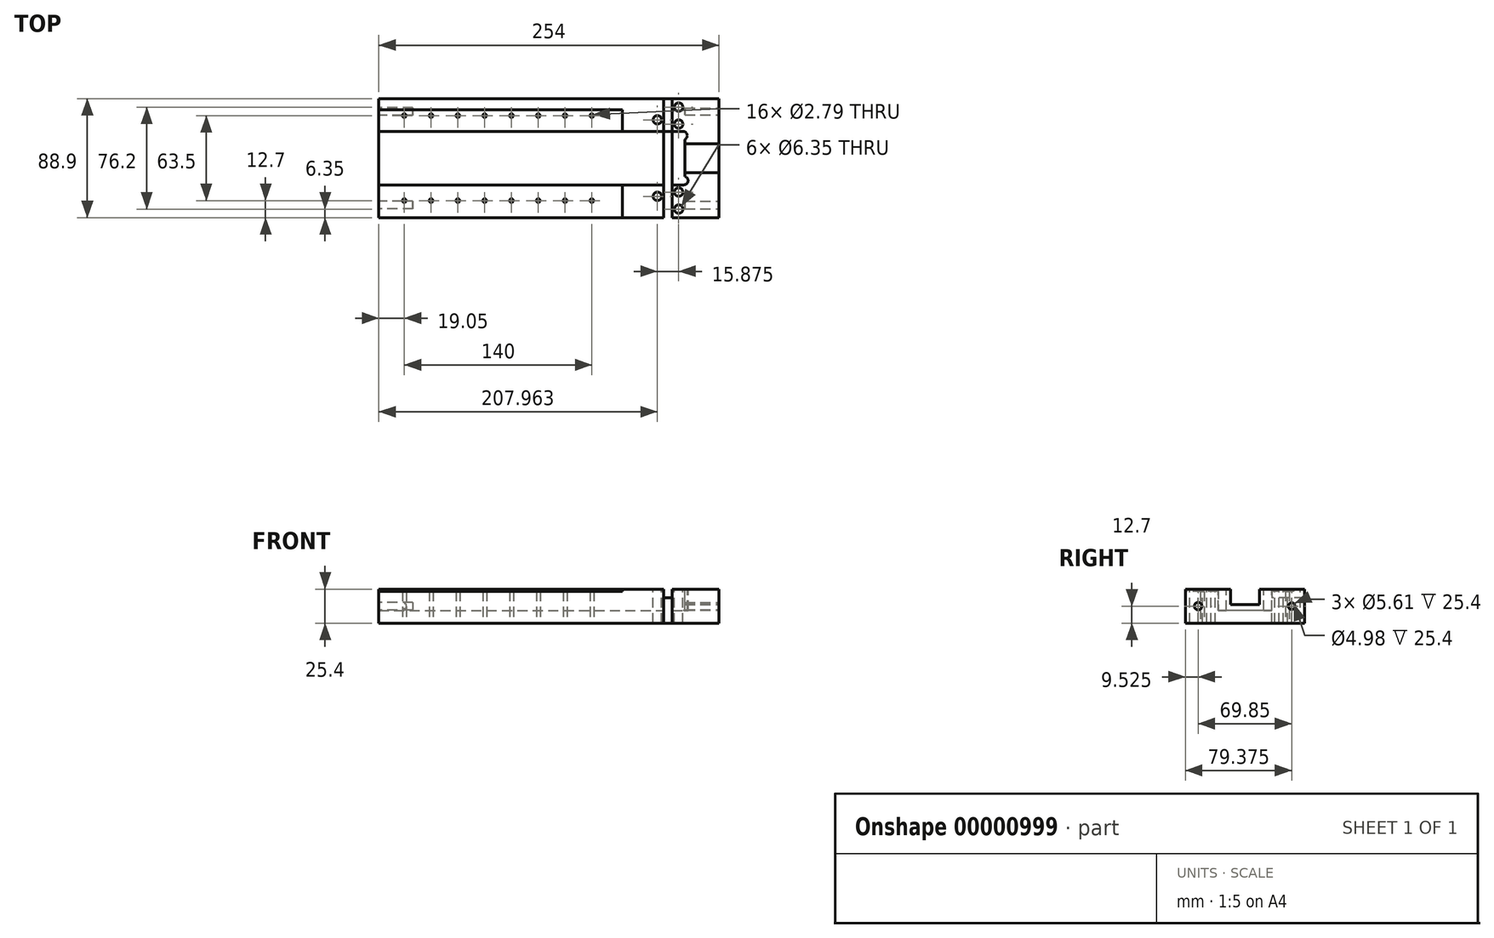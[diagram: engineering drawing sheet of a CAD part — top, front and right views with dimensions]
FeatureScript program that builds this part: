
annotation { "Feature Type Name" : "Feature", "Feature Type Description" : "" }
export const myFeature = defineFeature(function(context is Context, id is Id, definition is map)
    precondition{}
    {
        {
            var Q0;
            Q0=qCreatedBy(makeId("Top.planeOp"),FACE);
            var sketch = newSketch(context, id + "F0", { "sketchPlane" : qUnion([Q0])});
            skLineSegment(sketch, "E0.bottom", {"start": v(-127, 44.45) * mm, "end": v(127, 44.45) * mm});
            skLineSegment(sketch, "E0.top", {"start": v(-127, -44.45) * mm, "end": v(127, -44.45) * mm});
            skLineSegment(sketch, "E0.left", {"start": v(-127, 44.45) * mm, "end": v(-127, -44.45) * mm});
            skLineSegment(sketch, "E0.right", {"start": v(127, 44.45) * mm, "end": v(127, -44.45) * mm});
            skCircle(sketch, "E1", {"center": v(-107.95, -31.75) * mm, "radius": 1.4 * mm});
            skCircle(sketch, "E2", {"center": v(-107.95, 31.75) * mm, "radius": 1.4 * mm});
            skCircle(sketch, "E3", {"center": v(-27.95, 31.75) * mm, "radius": 1.4 * mm});
            skCircle(sketch, "E4", {"center": v(-87.95, 31.75) * mm, "radius": 1.4 * mm});
            skCircle(sketch, "E5", {"center": v(-67.95, 31.75) * mm, "radius": 1.4 * mm});
            skCircle(sketch, "E6", {"center": v(-47.95, 31.75) * mm, "radius": 1.4 * mm});
            skCircle(sketch, "E7", {"center": v(-7.95, 31.75) * mm, "radius": 1.4 * mm});
            skCircle(sketch, "E8", {"center": v(12.05, 31.75) * mm, "radius": 1.4 * mm});
            skCircle(sketch, "E9", {"center": v(32.05, 31.75) * mm, "radius": 1.4 * mm});
            skCircle(sketch, "E10", {"center": v(-87.95, -31.75) * mm, "radius": 1.4 * mm});
            skCircle(sketch, "E11", {"center": v(-67.95, -31.75) * mm, "radius": 1.4 * mm});
            skCircle(sketch, "E12", {"center": v(-47.95, -31.75) * mm, "radius": 1.4 * mm});
            skCircle(sketch, "E13", {"center": v(-27.95, -31.75) * mm, "radius": 1.4 * mm});
            skCircle(sketch, "E14", {"center": v(-7.95, -31.75) * mm, "radius": 1.4 * mm});
            skCircle(sketch, "E15", {"center": v(12.05, -31.75) * mm, "radius": 1.4 * mm});
            skCircle(sketch, "E16", {"center": v(32.05, -31.75) * mm, "radius": 1.4 * mm});
            skSolve(sketch);
        }
        {
            var Q0;
            Q0=makeQuery(id+"F0.imprint","IMPRINT",FACE,{"disambiguationData":[TD([[makeQuery(id+"F0.imprint","IMPRINT",EDGE,{"derivedFrom":sQuery(id+"F0.wireOp",EDGE,"E0.bottom")}),-1.0]])]});
            extrude(context, id + "F1", {"entities" : qUnion([Q0]), "depth" : 25.4 * mm});
        }
        {
            var Q0;
            Q0=makeQuery(id+"F1.opExtrude","CAP_FACE",FACE,{"disambiguationData":[OSD([sQuery(id+"F0.wireOp",EDGE,"E0.bottom"),sQuery(id+"F0.wireOp",EDGE,"E0.top"),sQuery(id+"F0.wireOp",EDGE,"E0.left"),sQuery(id+"F0.wireOp",EDGE,"E0.right"),sQuery(id+"F0.wireOp",EDGE,"E1"),sQuery(id+"F0.wireOp",EDGE,"E2"),sQuery(id+"F0.wireOp",EDGE,"E3"),sQuery(id+"F0.wireOp",EDGE,"E4"),sQuery(id+"F0.wireOp",EDGE,"E5"),sQuery(id+"F0.wireOp",EDGE,"E6"),sQuery(id+"F0.wireOp",EDGE,"E7"),sQuery(id+"F0.wireOp",EDGE,"E8"),sQuery(id+"F0.wireOp",EDGE,"E9"),sQuery(id+"F0.wireOp",EDGE,"E10"),sQuery(id+"F0.wireOp",EDGE,"E11"),sQuery(id+"F0.wireOp",EDGE,"E12"),sQuery(id+"F0.wireOp",EDGE,"E13"),sQuery(id+"F0.wireOp",EDGE,"E14"),sQuery(id+"F0.wireOp",EDGE,"E15"),sQuery(id+"F0.wireOp",EDGE,"E16")])],"isStart":false});
            var sketch = newSketch(context, id + "F2", { "sketchPlane" : qUnion([Q0])});
            skLineSegment(sketch, "E17.bottom", {"start": v(-127, 20) * mm, "end": v(100.1, 20) * mm});
            skLineSegment(sketch, "E17.top", {"start": v(-127, -20) * mm, "end": v(100.75, -20) * mm});
            skPoint(sketch, "E18.visualSharp", {"position": v(76.2, 20) * mm});
            skArc(sketch, "E18.filletArc", {"start": v(101.6, 14.02) * mm, "mid": v(103.18, 17.6) * mm, "end": v(100.1, 20) * mm});
            skPoint(sketch, "E19.visualSharp", {"position": v(76.2, -20) * mm});
            skArc(sketch, "E19.filletArc", {"start": v(100.75, -20) * mm, "mid": v(103.9, -17.25) * mm, "end": v(101.6, -13.77) * mm});
            skLineSegment(sketch, "E20", {"start": v(101.6, 14.02) * mm, "end": v(101.6, -13.77) * mm});
            skLineSegment(sketch, "E21", {"start": v(-127, 20) * mm, "end": v(-127, -20) * mm});
            skSolve(sketch);
        }
        {
            var Q0;
            Q0=makeQuery(id+"F2.imprint","IMPRINT",FACE,{"disambiguationData":[TD([[makeQuery(id+"F2.imprint","IMPRINT",EDGE,{"derivedFrom":sQuery(id+"F2.wireOp",EDGE,"E17.bottom")}),-1.0]])]});
            extrude(context, id + "F3", {"entities" : qUnion([Q0]), "operationType" : NewBodyOperationType.REMOVE, "oppositeDirection" : true, "depth" : 16 * mm});
        }
        {
            var Q0;
            Q0=makeQuery(id+"F1.opExtrude","CAP_FACE",FACE,{"disambiguationData":[OSD([sQuery(id+"F0.wireOp",EDGE,"E0.bottom"),sQuery(id+"F0.wireOp",EDGE,"E0.top"),sQuery(id+"F0.wireOp",EDGE,"E0.left"),sQuery(id+"F0.wireOp",EDGE,"E0.right"),sQuery(id+"F0.wireOp",EDGE,"E1"),sQuery(id+"F0.wireOp",EDGE,"E2"),sQuery(id+"F0.wireOp",EDGE,"E3"),sQuery(id+"F0.wireOp",EDGE,"E4"),sQuery(id+"F0.wireOp",EDGE,"E5"),sQuery(id+"F0.wireOp",EDGE,"E6"),sQuery(id+"F0.wireOp",EDGE,"E7"),sQuery(id+"F0.wireOp",EDGE,"E8"),sQuery(id+"F0.wireOp",EDGE,"E9"),sQuery(id+"F0.wireOp",EDGE,"E10"),sQuery(id+"F0.wireOp",EDGE,"E11"),sQuery(id+"F0.wireOp",EDGE,"E12"),sQuery(id+"F0.wireOp",EDGE,"E13"),sQuery(id+"F0.wireOp",EDGE,"E14"),sQuery(id+"F0.wireOp",EDGE,"E15"),sQuery(id+"F0.wireOp",EDGE,"E16")])],"isStart":false});
            var sketch = newSketch(context, id + "F4", { "sketchPlane" : qUnion([Q0])});
            skLineSegment(sketch, "E22.bottom", {"start": v(98.42, 10.8) * mm, "end": v(127, 10.8) * mm});
            skLineSegment(sketch, "E22.top", {"start": v(98.42, -10.8) * mm, "end": v(127, -10.8) * mm});
            skLineSegment(sketch, "E22.left", {"start": v(95.25, 7.62) * mm, "end": v(95.25, -7.62) * mm});
            skLineSegment(sketch, "E22.right", {"start": v(127, 10.8) * mm, "end": v(127, -10.8) * mm});
            skPoint(sketch, "E23.visualSharp", {"position": v(95.25, 10.8) * mm});
            skArc(sketch, "E23.filletArc", {"start": v(98.42, 10.8) * mm, "mid": v(96.18, 9.87) * mm, "end": v(95.25, 7.62) * mm});
            skPoint(sketch, "E24.visualSharp", {"position": v(95.25, -10.8) * mm});
            skArc(sketch, "E24.filletArc", {"start": v(95.25, -7.62) * mm, "mid": v(96.18, -9.87) * mm, "end": v(98.42, -10.8) * mm});
            skSolve(sketch);
        }
        {
            var Q0;
            {var subQ5=sQuery(id+"F4.wireOp",EDGE,"E22.right");Q0=makeQuery(id+"F4.imprint","IMPRINT",FACE,{"disambiguationData":[TD([[makeQuery(id+"F4.imprint","IMPRINT",EDGE,{"derivedFrom":subQ5}),-1.0]])]});}
            extrude(context, id + "F5", {"entities" : qUnion([Q0]), "operationType" : NewBodyOperationType.REMOVE, "oppositeDirection" : true, "depth" : 11.43 * mm});
        }
        {
            var Q0;
            {var subQ0=sQuery(id+"F0.wireOp",EDGE,"E0.bottom");var subQ1=sQuery(id+"F0.wireOp",EDGE,"E0.top");var subQ2=sQuery(id+"F0.wireOp",EDGE,"E0.left");var subQ3=sQuery(id+"F0.wireOp",EDGE,"E0.right");var subQ4=sQuery(id+"F0.wireOp",EDGE,"E1");var subQ5=sQuery(id+"F0.wireOp",EDGE,"E2");var subQ6=sQuery(id+"F0.wireOp",EDGE,"E3");var subQ7=sQuery(id+"F0.wireOp",EDGE,"E4");var subQ8=sQuery(id+"F0.wireOp",EDGE,"E5");var subQ9=sQuery(id+"F0.wireOp",EDGE,"E6");var subQ10=sQuery(id+"F0.wireOp",EDGE,"E7");var subQ11=sQuery(id+"F0.wireOp",EDGE,"E8");var subQ12=sQuery(id+"F0.wireOp",EDGE,"E9");var subQ13=sQuery(id+"F0.wireOp",EDGE,"E10");var subQ14=sQuery(id+"F0.wireOp",EDGE,"E11");var subQ15=sQuery(id+"F0.wireOp",EDGE,"E12");var subQ16=sQuery(id+"F0.wireOp",EDGE,"E13");var subQ17=sQuery(id+"F0.wireOp",EDGE,"E14");var subQ18=sQuery(id+"F0.wireOp",EDGE,"E15");var subQ19=sQuery(id+"F0.wireOp",EDGE,"E16");var subQ20=makeQuery(id+"F1.opExtrude","CAP_FACE",FACE,{"disambiguationData":[OSD([subQ0,subQ1,subQ2,subQ3,subQ4,subQ5,subQ6,subQ7,subQ8,subQ9,subQ10,subQ11,subQ12,subQ13,subQ14,subQ15,subQ16,subQ17,subQ18,subQ19])],"isStart":false});Q0=qUnion([makeQuery(id+"F5.boolean.opBoolean","SPLIT",FACE,{"disambiguationData":[TD([makeQuery(id+"F1.opExtrude","SWEPT_FACE",FACE,{"disambiguationData":[OSD([subQ0])]})])],"derivedFrom":subQ20}),makeQuery(id+"F5.boolean.opBoolean","SPLIT",FACE,{"disambiguationData":[TD([makeQuery(id+"F1.opExtrude","SWEPT_FACE",FACE,{"disambiguationData":[OSD([subQ1])]})])],"derivedFrom":subQ20})]);}
            var sketch = newSketch(context, id + "F6", { "sketchPlane" : qUnion([Q0])});
            skCircle(sketch, "E25", {"center": v(96.84, 38.1) * mm, "radius": 3.18 * mm});
            skLineSegment(sketch, "E26", {"start": v(76.2, 47.2) * mm, "end": v(76.2, -48.73) * mm, "construction": true});
            skCircle(sketch, "E27", {"center": v(80.96, 28.58) * mm, "radius": 3.18 * mm});
            skCircle(sketch, "E28", {"center": v(80.96, -28.57) * mm, "radius": 3.18 * mm});
            skCircle(sketch, "E29", {"center": v(96.84, -38.1) * mm, "radius": 3.18 * mm});
            skLineSegment(sketch, "E30", {"start": v(101.6, 52.36) * mm, "end": v(101.6, -69.51) * mm, "construction": true});
            skCircle(sketch, "E31", {"center": v(96.84, 25.4) * mm, "radius": 3.18 * mm});
            skCircle(sketch, "E32", {"center": v(96.84, -25.4) * mm, "radius": 3.18 * mm});
            skLineSegment(sketch, "E33.bottom", {"start": v(85.72, 46.37) * mm, "end": v(92.07, 46.37) * mm});
            skLineSegment(sketch, "E33.top", {"start": v(85.72, -47.17) * mm, "end": v(92.08, -47.17) * mm});
            skLineSegment(sketch, "E33.left", {"start": v(85.72, 46.37) * mm, "end": v(85.72, -47.17) * mm});
            skLineSegment(sketch, "E33.right", {"start": v(92.07, 46.37) * mm, "end": v(92.07, -47.17) * mm});
            skPoint(sketch, "E34", {"position": v(88.9, 46.37) * mm});
            skSolve(sketch);
        }
        {
            var Q0;
            Q0=makeQuery(id+"F6.imprint","IMPRINT",FACE,{"disambiguationData":[TD([[makeQuery(id+"F6.imprint","IMPRINT",EDGE,{"derivedFrom":sQuery(id+"F6.wireOp",EDGE,"E25")}),1.0]])]});
            var Q1;
            Q1=makeQuery(id+"F6.imprint","IMPRINT",FACE,{"disambiguationData":[TD([[makeQuery(id+"F6.imprint","IMPRINT",EDGE,{"derivedFrom":sQuery(id+"F6.wireOp",EDGE,"E27")}),1.0]])]});
            var Q2;
            Q2=makeQuery(id+"F6.imprint","IMPRINT",FACE,{"disambiguationData":[TD([[makeQuery(id+"F6.imprint","IMPRINT",EDGE,{"derivedFrom":sQuery(id+"F6.wireOp",EDGE,"E31")}),1.0]])]});
            var Q3;
            Q3=makeQuery(id+"F6.imprint","IMPRINT",FACE,{"disambiguationData":[TD([[makeQuery(id+"F6.imprint","IMPRINT",EDGE,{"derivedFrom":sQuery(id+"F6.wireOp",EDGE,"E28")}),1.0]])]});
            var Q4;
            Q4=makeQuery(id+"F6.imprint","IMPRINT",FACE,{"disambiguationData":[TD([[makeQuery(id+"F6.imprint","IMPRINT",EDGE,{"derivedFrom":sQuery(id+"F6.wireOp",EDGE,"E29")}),1.0]])]});
            var Q5;
            Q5=makeQuery(id+"F6.imprint","IMPRINT",FACE,{"disambiguationData":[TD([[makeQuery(id+"F6.imprint","IMPRINT",EDGE,{"derivedFrom":sQuery(id+"F6.wireOp",EDGE,"E32")}),1.0]])]});
            var Q6;
            {var subQ5=sQuery(id+"F6.wireOp",EDGE,"E33.top");Q6=makeQuery(id+"F6.imprint","IMPRINT",FACE,{"disambiguationData":[TD([[makeQuery(id+"F6.imprint","IMPRINT",EDGE,{"derivedFrom":subQ5}),1.0]])]});}
            extrude(context, id + "F7", {"entities" : qUnion([Q0, Q1, Q2, Q3, Q4, Q5, Q6]), "operationType" : NewBodyOperationType.REMOVE, "endBound" : BoundingType.THROUGH_ALL, "oppositeDirection" : true, "depth" : 25.4 * mm});
        }
        {
            var Q0;
            Q0=makeQuery(id+"F1.opExtrude","SWEPT_FACE",FACE,{"disambiguationData":[OSD([sQuery(id+"F0.wireOp",EDGE,"E0.right")])]});
            var sketch = newSketch(context, id + "F8", { "sketchPlane" : qUnion([Q0])});
            skCircle(sketch, "E35", {"center": v(-34.93, 12.7) * mm, "radius": 2.8 * mm});
            skCircle(sketch, "E36", {"center": v(34.92, 12.7) * mm, "radius": 2.5 * mm});
            skSolve(sketch);
        }
        {
            var Q0;
            Q0=makeQuery(id+"F8.imprint","IMPRINT",FACE,{"disambiguationData":[TD([[makeQuery(id+"F8.imprint","IMPRINT",EDGE,{"derivedFrom":sQuery(id+"F8.wireOp",EDGE,"E35")}),1.0]])]});
            var Q1;
            Q1=makeQuery(id+"F8.imprint","IMPRINT",FACE,{"disambiguationData":[TD([[makeQuery(id+"F8.imprint","IMPRINT",EDGE,{"derivedFrom":sQuery(id+"F8.wireOp",EDGE,"E36")}),1.0]])]});
            var Q2;
            Q2=makeQuery(id+"F8.imprint","IMPRINT",FACE,{"disambiguationData":[TD([[makeQuery(id+"F8.imprint","IMPRINT",EDGE,{"derivedFrom":sQuery(id+"F8.wireOp",EDGE,"de399b29-484e-4ea1-890b-471df8b64df3")}),1.0]])]});
            var Q3;
            Q3=makeQuery(id+"F8.imprint","IMPRINT",FACE,{"disambiguationData":[TD([[makeQuery(id+"F8.imprint","IMPRINT",EDGE,{"derivedFrom":sQuery(id+"F8.wireOp",EDGE,"e27d1595-5bf9-4a61-a629-74f22b92437e")}),1.0]])]});
            extrude(context, id + "F9", {"entities" : qUnion([Q0, Q1, Q2, Q3]), "operationType" : NewBodyOperationType.REMOVE, "oppositeDirection" : true, "depth" : 25.4 * mm});
        }
        {
            var Q0;
            {var subQ0=makeQuery(id+"F1.opExtrude","CAP_EDGE",EDGE,{"disambiguationData":[OSD([sQuery(id+"F0.wireOp",EDGE,"E0.bottom")])],"isStart":false});var subQ3=sQuery(id+"F6.wireOp",EDGE,"E33.left");var subQ4=makeQuery(id+"F6.imprint","INTERSECT",VERTEX,{"derivedFrom":[subQ0,subQ3]});var subQ6=sQuery(id+"F6.wireOp",EDGE,"E33.bottom");var subQ11=sQuery(id+"F6.wireOp",EDGE,"E33.top");var subQ12=makeQuery(id+"F3.boolean.opBoolean","COPY",EDGE,{"derivedFrom":makeQuery(id+"F3.opExtrude","CAP_EDGE",EDGE,{"disambiguationData":[OSD([sQuery(id+"F2.wireOp",EDGE,"E17.bottom")])],"isStart":true})});var subQ14=makeQuery(id+"F6.imprint","INTERSECT",VERTEX,{"derivedFrom":[subQ12,subQ3]});var subQ16=makeQuery(id+"F3.boolean.opBoolean","COPY",EDGE,{"derivedFrom":makeQuery(id+"F3.opExtrude","CAP_EDGE",EDGE,{"disambiguationData":[OSD([sQuery(id+"F2.wireOp",EDGE,"E17.top")])],"isStart":true})});var subQ18=makeQuery(id+"F6.imprint","INTERSECT",VERTEX,{"derivedFrom":[subQ16,subQ3]});Q0=qUnion([makeQuery(id+"F6.imprint","IMPRINT",FACE,{"disambiguationData":[TD([[makeQuery(id+"F6.imprint","IMPRINT",EDGE,{"derivedFrom":sQuery(id+"F6.wireOp",EDGE,"E25")}),1.0]])]}),makeQuery(id+"F6.imprint","IMPRINT",FACE,{"disambiguationData":[TD([[makeQuery(id+"F6.imprint","IMPRINT",EDGE,{"derivedFrom":sQuery(id+"F6.wireOp",EDGE,"E27")}),1.0]])]}),makeQuery(id+"F6.imprint","IMPRINT",FACE,{"disambiguationData":[TD([[makeQuery(id+"F6.imprint","IMPRINT",EDGE,{"derivedFrom":sQuery(id+"F6.wireOp",EDGE,"E28")}),1.0]])]}),makeQuery(id+"F6.imprint","IMPRINT",FACE,{"disambiguationData":[TD([[makeQuery(id+"F6.imprint","IMPRINT",EDGE,{"derivedFrom":sQuery(id+"F6.wireOp",EDGE,"E29")}),1.0]])]}),makeQuery(id+"F6.imprint","IMPRINT",FACE,{"disambiguationData":[TD([[makeQuery(id+"F6.imprint","IMPRINT",EDGE,{"derivedFrom":sQuery(id+"F6.wireOp",EDGE,"E31")}),1.0]])]}),makeQuery(id+"F6.imprint","IMPRINT",FACE,{"disambiguationData":[TD([[makeQuery(id+"F6.imprint","IMPRINT",EDGE,{"derivedFrom":sQuery(id+"F6.wireOp",EDGE,"E32")}),1.0]])]}),makeQuery(id+"F6.imprint","IMPRINT",FACE,{"disambiguationData":[TD([[makeQuery(id+"F6.imprint","IMPRINT",EDGE,{"derivedFrom":subQ6}),-1.0]])]}),makeQuery(id+"F6.imprint","IMPRINT",FACE,{"disambiguationData":[TD([[makeQuery(id+"F6.imprint","IMPRINT",EDGE,{"derivedFrom":subQ11}),1.0]])]}),makeQuery(id+"F6.imprint","IMPRINT",FACE,{"disambiguationData":[TD([[makeQuery(id+"F6.imprint","IMPRINT",EDGE,{"disambiguationData":[TD([[subQ14,-1.0]])],"derivedFrom":subQ3}),1.0]])]}),makeQuery(id+"F6.imprint","IMPRINT",FACE,{"disambiguationData":[TD([[makeQuery(id+"F6.imprint","IMPRINT",EDGE,{"disambiguationData":[TD([[subQ4,-1.0]])],"derivedFrom":subQ3}),1.0]])]}),makeQuery(id+"F6.imprint","IMPRINT",FACE,{"disambiguationData":[TD([[makeQuery(id+"F6.imprint","IMPRINT",EDGE,{"disambiguationData":[TD([[subQ18,-1.0]])],"derivedFrom":subQ3}),1.0]])]})]);}
            extrude(context, id + "F10", {"entities" : qUnion([Q0]), "operationType" : NewBodyOperationType.REMOVE, "oppositeDirection" : true, "depth" : 6.35 * mm});
        }
        {
            var Q0;
            Q0=makeQuery(id+"F1.opExtrude","SWEPT_FACE",FACE,{"disambiguationData":[OSD([sQuery(id+"F0.wireOp",EDGE,"E0.left")])]});
            var sketch = newSketch(context, id + "F11", { "sketchPlane" : qUnion([Q0])});
            skCircle(sketch, "E37", {"center": v(-34.93, 12.7) * mm, "radius": 2.8 * mm});
            skCircle(sketch, "E38", {"center": v(34.92, 12.7) * mm, "radius": 2.8 * mm});
            skSolve(sketch);
        }
        {
            var Q0;
            {Q0=qUnion([makeQuery(id+"F11.imprint","IMPRINT",FACE,{"disambiguationData":[TD([[makeQuery(id+"F11.imprint","IMPRINT",EDGE,{"derivedFrom":sQuery(id+"F11.wireOp",EDGE,"E37")}),1.0]])]}),makeQuery(id+"F11.imprint","IMPRINT",FACE,{"disambiguationData":[TD([[makeQuery(id+"F11.imprint","IMPRINT",EDGE,{"derivedFrom":sQuery(id+"F11.wireOp",EDGE,"E38")}),1.0]])]})]);}
            extrude(context, id + "F12", {"entities" : qUnion([Q0]), "operationType" : NewBodyOperationType.REMOVE, "oppositeDirection" : true, "depth" : 25.4 * mm});
        }
        {
            var Q0;
            {var subQ4=sQuery(id+"F2.wireOp",EDGE,"E17.bottom");Q0=makeQuery(id+"F2.imprint","IMPRINT",FACE,{"disambiguationData":[TD([[makeQuery(id+"F2.imprint","IMPRINT",EDGE,{"derivedFrom":subQ4}),1.0]])]});}
            var sketch = newSketch(context, id + "F13", { "sketchPlane" : qUnion([Q0])});
            skLineSegment(sketch, "E39.bottom", {"start": v(-136.7, 36.25) * mm, "end": v(54.9, 36.25) * mm});
            skLineSegment(sketch, "E39.top", {"start": v(-136.7, -46.3) * mm, "end": v(54.9, -46.3) * mm});
            skLineSegment(sketch, "E39.left", {"start": v(-136.7, 36.25) * mm, "end": v(-136.7, -46.3) * mm});
            skLineSegment(sketch, "E39.right", {"start": v(54.9, 36.25) * mm, "end": v(54.9, -46.3) * mm});
            skSolve(sketch);
        }
        {
            var Q0;
            {var subQ0=makeQuery(id+"F13.imprint","IMPRINT",EDGE,{"derivedFrom":makeQuery(id+"F2.imprint","IMPRINT",EDGE,{"derivedFrom":makeQuery(id+"F1.opExtrude","CAP_EDGE",EDGE,{"disambiguationData":[OSD([sQuery(id+"F0.wireOp",EDGE,"E1")])],"isStart":false})})});var subQ1=makeQuery(id+"F13.imprint","IMPRINT",EDGE,{"derivedFrom":makeQuery(id+"F2.imprint","IMPRINT",EDGE,{"derivedFrom":makeQuery(id+"F1.opExtrude","CAP_EDGE",EDGE,{"disambiguationData":[OSD([sQuery(id+"F0.wireOp",EDGE,"E2")])],"isStart":false})})});var subQ2=makeQuery(id+"F13.imprint","IMPRINT",EDGE,{"derivedFrom":makeQuery(id+"F2.imprint","IMPRINT",EDGE,{"derivedFrom":makeQuery(id+"F1.opExtrude","CAP_EDGE",EDGE,{"disambiguationData":[OSD([sQuery(id+"F0.wireOp",EDGE,"E3")])],"isStart":false})})});var subQ3=makeQuery(id+"F13.imprint","IMPRINT",EDGE,{"derivedFrom":makeQuery(id+"F2.imprint","IMPRINT",EDGE,{"derivedFrom":makeQuery(id+"F1.opExtrude","CAP_EDGE",EDGE,{"disambiguationData":[OSD([sQuery(id+"F0.wireOp",EDGE,"E4")])],"isStart":false})})});var subQ4=makeQuery(id+"F13.imprint","IMPRINT",EDGE,{"derivedFrom":makeQuery(id+"F2.imprint","IMPRINT",EDGE,{"derivedFrom":makeQuery(id+"F1.opExtrude","CAP_EDGE",EDGE,{"disambiguationData":[OSD([sQuery(id+"F0.wireOp",EDGE,"E5")])],"isStart":false})})});var subQ5=makeQuery(id+"F13.imprint","IMPRINT",EDGE,{"derivedFrom":makeQuery(id+"F2.imprint","IMPRINT",EDGE,{"derivedFrom":makeQuery(id+"F1.opExtrude","CAP_EDGE",EDGE,{"disambiguationData":[OSD([sQuery(id+"F0.wireOp",EDGE,"E6")])],"isStart":false})})});var subQ6=makeQuery(id+"F13.imprint","IMPRINT",EDGE,{"derivedFrom":makeQuery(id+"F2.imprint","IMPRINT",EDGE,{"derivedFrom":makeQuery(id+"F1.opExtrude","CAP_EDGE",EDGE,{"disambiguationData":[OSD([sQuery(id+"F0.wireOp",EDGE,"E7")])],"isStart":false})})});var subQ7=makeQuery(id+"F13.imprint","IMPRINT",EDGE,{"derivedFrom":makeQuery(id+"F2.imprint","IMPRINT",EDGE,{"derivedFrom":makeQuery(id+"F1.opExtrude","CAP_EDGE",EDGE,{"disambiguationData":[OSD([sQuery(id+"F0.wireOp",EDGE,"E8")])],"isStart":false})})});var subQ8=makeQuery(id+"F13.imprint","IMPRINT",EDGE,{"derivedFrom":makeQuery(id+"F2.imprint","IMPRINT",EDGE,{"derivedFrom":makeQuery(id+"F1.opExtrude","CAP_EDGE",EDGE,{"disambiguationData":[OSD([sQuery(id+"F0.wireOp",EDGE,"E9")])],"isStart":false})})});var subQ9=makeQuery(id+"F13.imprint","IMPRINT",EDGE,{"derivedFrom":makeQuery(id+"F2.imprint","IMPRINT",EDGE,{"derivedFrom":makeQuery(id+"F1.opExtrude","CAP_EDGE",EDGE,{"disambiguationData":[OSD([sQuery(id+"F0.wireOp",EDGE,"E10")])],"isStart":false})})});var subQ10=makeQuery(id+"F13.imprint","IMPRINT",EDGE,{"derivedFrom":makeQuery(id+"F2.imprint","IMPRINT",EDGE,{"derivedFrom":makeQuery(id+"F1.opExtrude","CAP_EDGE",EDGE,{"disambiguationData":[OSD([sQuery(id+"F0.wireOp",EDGE,"E11")])],"isStart":false})})});var subQ11=makeQuery(id+"F13.imprint","IMPRINT",EDGE,{"derivedFrom":makeQuery(id+"F2.imprint","IMPRINT",EDGE,{"derivedFrom":makeQuery(id+"F1.opExtrude","CAP_EDGE",EDGE,{"disambiguationData":[OSD([sQuery(id+"F0.wireOp",EDGE,"E12")])],"isStart":false})})});var subQ12=makeQuery(id+"F13.imprint","IMPRINT",EDGE,{"derivedFrom":makeQuery(id+"F2.imprint","IMPRINT",EDGE,{"derivedFrom":makeQuery(id+"F1.opExtrude","CAP_EDGE",EDGE,{"disambiguationData":[OSD([sQuery(id+"F0.wireOp",EDGE,"E13")])],"isStart":false})})});var subQ13=makeQuery(id+"F13.imprint","IMPRINT",EDGE,{"derivedFrom":makeQuery(id+"F2.imprint","IMPRINT",EDGE,{"derivedFrom":makeQuery(id+"F1.opExtrude","CAP_EDGE",EDGE,{"disambiguationData":[OSD([sQuery(id+"F0.wireOp",EDGE,"E14")])],"isStart":false})})});var subQ14=makeQuery(id+"F13.imprint","IMPRINT",EDGE,{"derivedFrom":makeQuery(id+"F2.imprint","IMPRINT",EDGE,{"derivedFrom":makeQuery(id+"F1.opExtrude","CAP_EDGE",EDGE,{"disambiguationData":[OSD([sQuery(id+"F0.wireOp",EDGE,"E15")])],"isStart":false})})});var subQ15=makeQuery(id+"F13.imprint","IMPRINT",EDGE,{"derivedFrom":makeQuery(id+"F2.imprint","IMPRINT",EDGE,{"derivedFrom":makeQuery(id+"F1.opExtrude","CAP_EDGE",EDGE,{"disambiguationData":[OSD([sQuery(id+"F0.wireOp",EDGE,"E16")])],"isStart":false})})});var subQ39=sQuery(id+"F13.wireOp",EDGE,"E39.top");Q0=qUnion([makeQuery(id+"F13.imprint","IMPRINT",FACE,{"disambiguationData":[TD([[subQ0,1.0]])]}),makeQuery(id+"F13.imprint","IMPRINT",FACE,{"disambiguationData":[TD([[subQ1,1.0]])]}),makeQuery(id+"F13.imprint","IMPRINT",FACE,{"disambiguationData":[TD([[subQ2,1.0]])]}),makeQuery(id+"F13.imprint","IMPRINT",FACE,{"disambiguationData":[TD([[subQ3,1.0]])]}),makeQuery(id+"F13.imprint","IMPRINT",FACE,{"disambiguationData":[TD([[subQ4,1.0]])]}),makeQuery(id+"F13.imprint","IMPRINT",FACE,{"disambiguationData":[TD([[subQ5,1.0]])]}),makeQuery(id+"F13.imprint","IMPRINT",FACE,{"disambiguationData":[TD([[subQ6,1.0]])]}),makeQuery(id+"F13.imprint","IMPRINT",FACE,{"disambiguationData":[TD([[subQ7,1.0]])]}),makeQuery(id+"F13.imprint","IMPRINT",FACE,{"disambiguationData":[TD([[subQ8,1.0]])]}),makeQuery(id+"F13.imprint","IMPRINT",FACE,{"disambiguationData":[TD([[subQ9,1.0]])]}),makeQuery(id+"F13.imprint","IMPRINT",FACE,{"disambiguationData":[TD([[subQ10,1.0]])]}),makeQuery(id+"F13.imprint","IMPRINT",FACE,{"disambiguationData":[TD([[subQ11,1.0]])]}),makeQuery(id+"F13.imprint","IMPRINT",FACE,{"disambiguationData":[TD([[subQ12,1.0]])]}),makeQuery(id+"F13.imprint","IMPRINT",FACE,{"disambiguationData":[TD([[subQ13,1.0]])]}),makeQuery(id+"F13.imprint","IMPRINT",FACE,{"disambiguationData":[TD([[subQ14,1.0]])]}),makeQuery(id+"F13.imprint","IMPRINT",FACE,{"disambiguationData":[TD([[subQ15,1.0]])]}),makeQuery(id+"F13.imprint","IMPRINT",FACE,{"disambiguationData":[TD([[subQ1,-1.0]])]}),makeQuery(id+"F13.imprint","IMPRINT",FACE,{"disambiguationData":[TD([[subQ0,-1.0]])]}),makeQuery(id+"F13.imprint","IMPRINT",FACE,{"disambiguationData":[TD([[makeQuery(id+"F13.imprint","IMPRINT",EDGE,{"derivedFrom":subQ39}),1.0]])]})]);}
            extrude(context, id + "F14", {"entities" : qUnion([Q0]), "operationType" : NewBodyOperationType.REMOVE, "oppositeDirection" : true, "depth" : 1.59 * mm});
        }
    });
